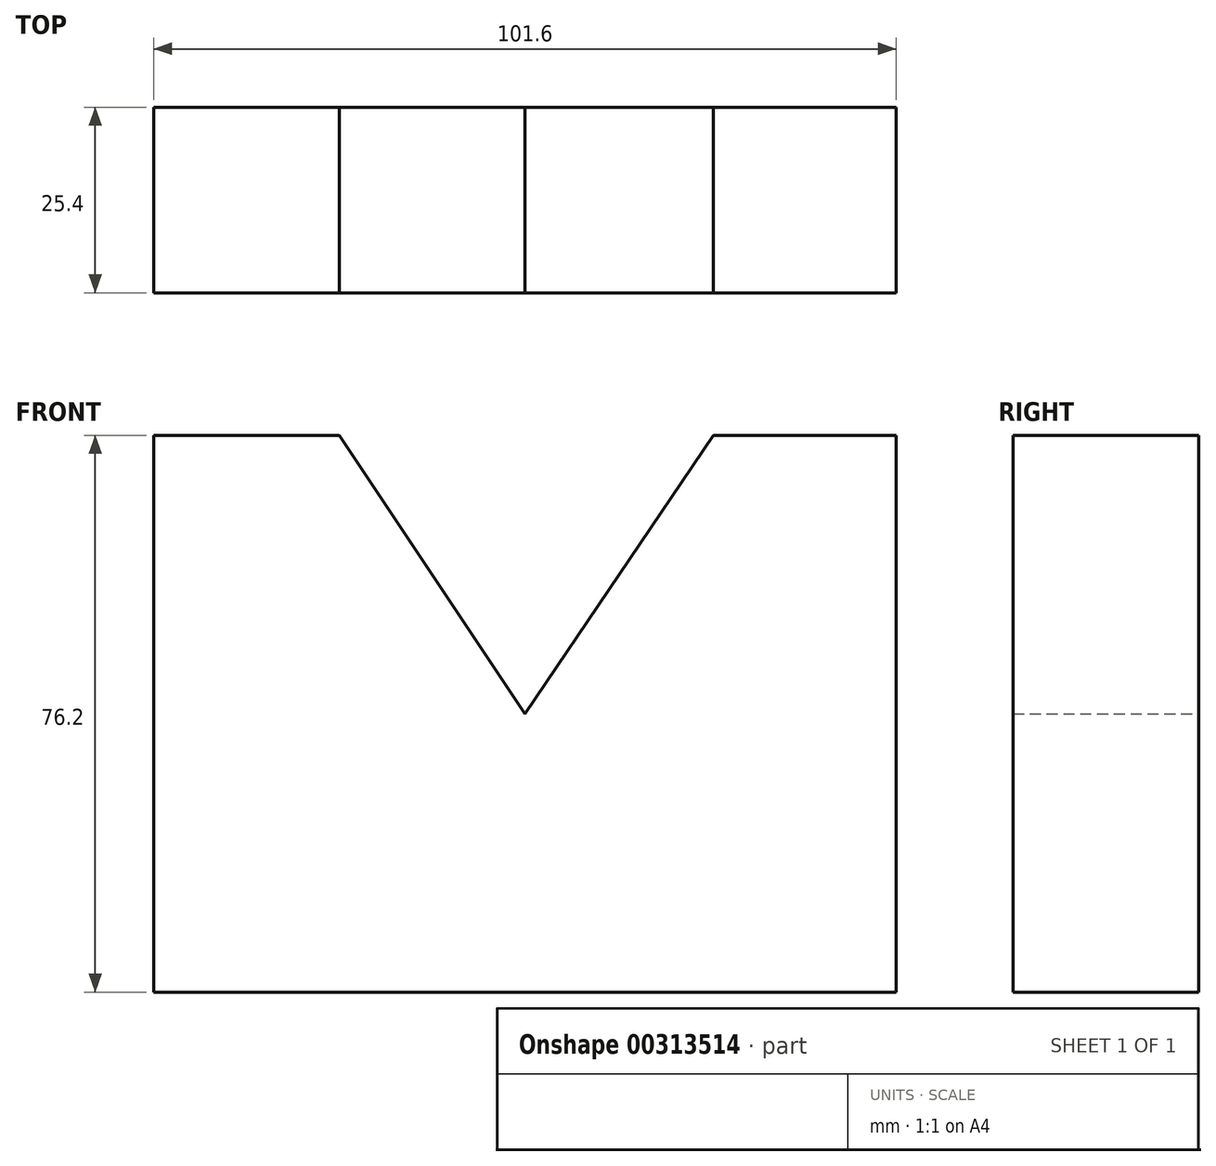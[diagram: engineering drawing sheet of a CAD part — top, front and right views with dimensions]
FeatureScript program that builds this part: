
annotation { "Feature Type Name" : "Feature", "Feature Type Description" : "" }
export const myFeature = defineFeature(function(context is Context, id is Id, definition is map)
    precondition{}
    {
        {
            var Q0;
            Q0=qCreatedBy(makeId("Front.planeOp"),FACE);
            var sketch = newSketch(context, id + "F0", { "sketchPlane" : qUnion([Q0])});
            skLineSegment(sketch, "E0", {"start": v(-49.49, -46.75) * mm, "end": v(52.11, -46.75) * mm});
            skLineSegment(sketch, "E1", {"start": v(52.11, -46.75) * mm, "end": v(52.11, 29.45) * mm});
            skLineSegment(sketch, "E2", {"start": v(52.11, 29.45) * mm, "end": v(27.11, 29.45) * mm});
            skLineSegment(sketch, "E3", {"start": v(-49.49, -46.75) * mm, "end": v(-49.49, 29.45) * mm});
            skLineSegment(sketch, "E4", {"start": v(-49.49, 29.45) * mm, "end": v(-24.09, 29.45) * mm});
            skPoint(sketch, "E5.startSnap0", {"position": v(1.31, -46.75) * mm});
            skLineSegment(sketch, "E6", {"start": v(-24.09, 29.45) * mm, "end": v(1.31, -8.65) * mm});
            skLineSegment(sketch, "E7", {"start": v(1.31, -8.65) * mm, "end": v(27.11, 29.45) * mm});
            skSolve(sketch);
        }
        {
            var Q0;
            Q0=makeQuery(id+"F0.imprint","IMPRINT",FACE,{"disambiguationData":[TD([[makeQuery(id+"F0.imprint","IMPRINT",EDGE,{"derivedFrom":sQuery(id+"F0.wireOp",EDGE,"E0")}),1.0]])]});
            extrude(context, id + "F1", {"entities" : qUnion([Q0]), "depth" : 25.4 * mm});
        }
    });
